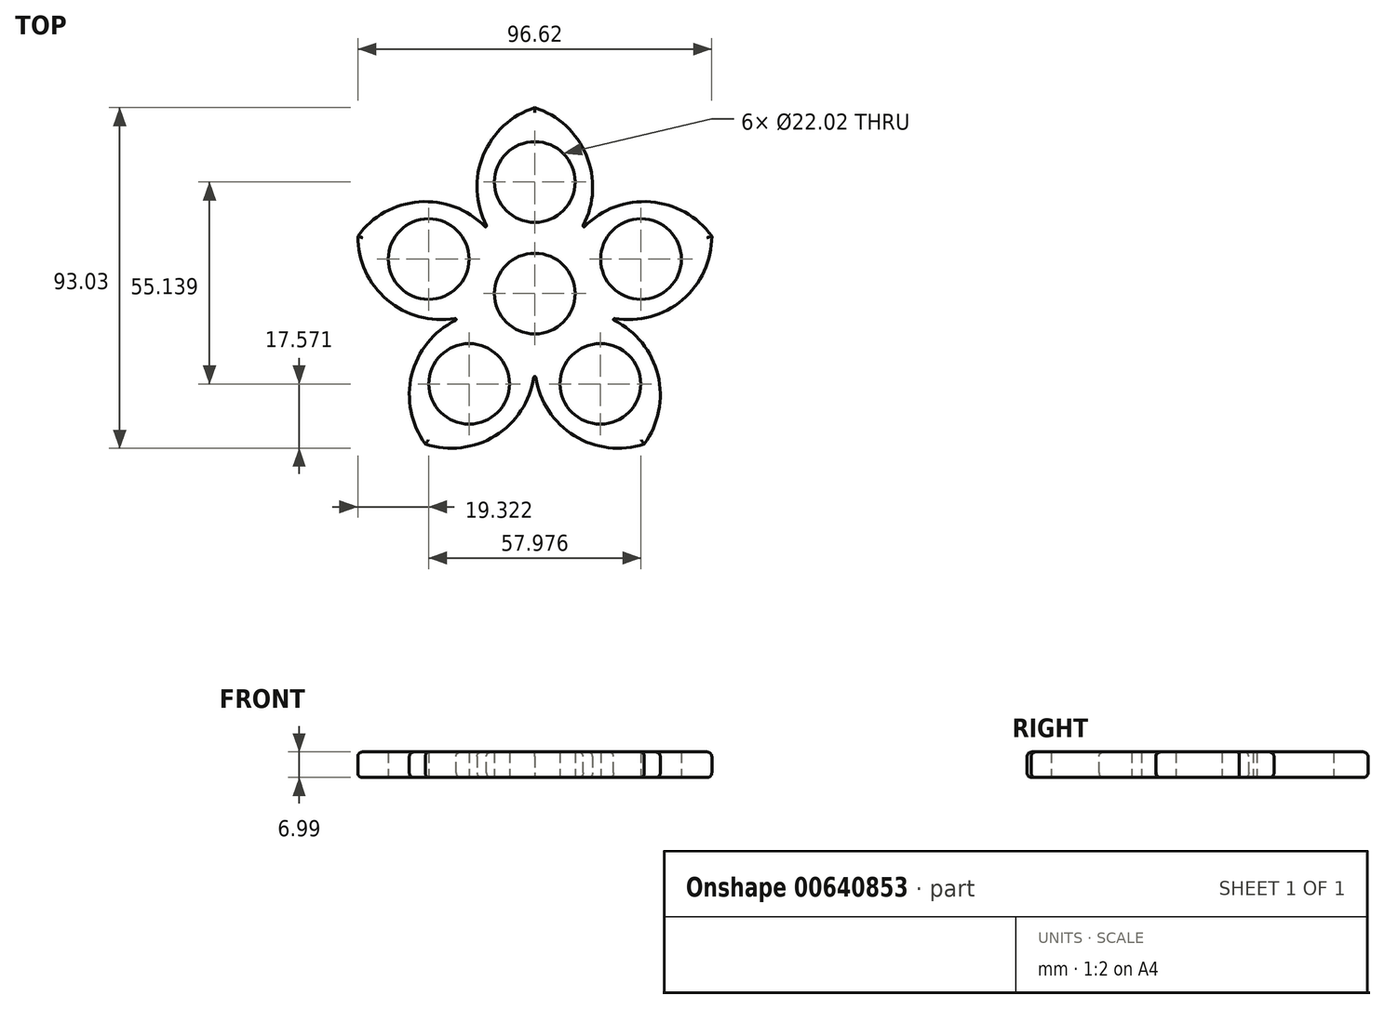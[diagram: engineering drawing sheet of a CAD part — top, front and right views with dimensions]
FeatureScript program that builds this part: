
annotation { "Feature Type Name" : "Feature", "Feature Type Description" : "" }
export const myFeature = defineFeature(function(context is Context, id is Id, definition is map)
    precondition{}
    {
        {
            var Q0;
            Q0=qCreatedBy(makeId("Top.planeOp"),FACE);
            var sketch = newSketch(context, id + "F0", { "sketchPlane" : qUnion([Q0])});
            skCircle(sketch, "E0", {"center": v(0, 0) * mm, "radius": 11.01 * mm});
            skCircle(sketch, "E1", {"center": v(0, 30.48) * mm, "radius": 11.01 * mm});
            skCircle(sketch, "E2", {"center": v(28.99, 9.42) * mm, "radius": 11.01 * mm});
            skCircle(sketch, "E3", {"center": v(17.92, -24.66) * mm, "radius": 11.01 * mm});
            skCircle(sketch, "E4", {"center": v(-17.92, -24.66) * mm, "radius": 11.01 * mm});
            skCircle(sketch, "E5", {"center": v(-28.99, 9.42) * mm, "radius": 11.01 * mm});
            skLineSegment(sketch, "E6", {"start": v(-28.99, 9.42) * mm, "end": v(0, 0) * mm});
            skLineSegment(sketch, "E7", {"start": v(0, 0) * mm, "end": v(0, 30.48) * mm});
            skLineSegment(sketch, "E8", {"start": v(28.99, 9.42) * mm, "end": v(0, 0) * mm});
            skLineSegment(sketch, "E9", {"start": v(-17.92, -24.66) * mm, "end": v(0, 0) * mm});
            skLineSegment(sketch, "E10", {"start": v(17.92, -24.66) * mm, "end": v(0, 0) * mm});
            skCircle(sketch, "E11", {"center": v(0, 0) * mm, "radius": 19.47 * mm});
            skLineSegment(sketch, "E12", {"start": v(0, 0) * mm, "end": v(0, -19.47) * mm});
            skLineSegment(sketch, "E13", {"start": v(0, -19.47) * mm, "end": v(0, 0) * mm});
            skLineSegment(sketch, "E14", {"start": v(0, 0) * mm, "end": v(18.52, -6.02) * mm});
            skLineSegment(sketch, "E15", {"start": v(18.52, -6.02) * mm, "end": v(0, 0) * mm});
            skLineSegment(sketch, "E16", {"start": v(-11.44, 15.75) * mm, "end": v(0, 0) * mm});
            skLineSegment(sketch, "E17", {"start": v(0, 0) * mm, "end": v(11.44, 15.75) * mm});
            skLineSegment(sketch, "E18", {"start": v(11.44, 15.75) * mm, "end": v(0, 0) * mm});
            skLineSegment(sketch, "E19", {"start": v(-18.52, -6.02) * mm, "end": v(0, 0) * mm});
            skLineSegment(sketch, "E20", {"start": v(0, 50.8) * mm, "end": v(0, 0) * mm});
            skLineSegment(sketch, "E21", {"start": v(0, 0) * mm, "end": v(-48.31, 15.7) * mm});
            skLineSegment(sketch, "E22", {"start": v(0, 0) * mm, "end": v(29.86, -41.1) * mm});
            skLineSegment(sketch, "E23", {"start": v(0, 0) * mm, "end": v(48.31, 15.7) * mm});
            skLineSegment(sketch, "E24", {"start": v(0, 0) * mm, "end": v(-29.86, -41.1) * mm});
            skArc(sketch, "E25", {"start": v(-48.31, 15.7) * mm, "mid": v(-38.96, -2.76) * mm, "end": v(-18.52, -6.02) * mm});
            skArc(sketch, "E26", {"start": v(-11.44, 15.75) * mm, "mid": v(-29.9, 25.13) * mm, "end": v(-48.31, 15.7) * mm});
            skArc(sketch, "E27", {"start": v(0, 50.8) * mm, "mid": v(-14.67, 36.2) * mm, "end": v(-11.44, 15.75) * mm});
            skArc(sketch, "E28", {"start": v(11.44, 15.75) * mm, "mid": v(14.67, 36.2) * mm, "end": v(0, 50.8) * mm});
            skArc(sketch, "E29", {"start": v(48.31, 15.7) * mm, "mid": v(29.9, 25.13) * mm, "end": v(11.44, 15.75) * mm});
            skArc(sketch, "E30", {"start": v(18.52, -6.02) * mm, "mid": v(38.96, -2.76) * mm, "end": v(48.31, 15.7) * mm});
            skArc(sketch, "E31", {"start": v(-18.52, -6.02) * mm, "mid": v(-33.14, -20.66) * mm, "end": v(-29.86, -41.1) * mm});
            skArc(sketch, "E32", {"start": v(-29.86, -41.1) * mm, "mid": v(-9.4, -37.9) * mm, "end": v(0, -19.47) * mm});
            skArc(sketch, "E33", {"start": v(0, -19.47) * mm, "mid": v(9.4, -37.9) * mm, "end": v(29.86, -41.1) * mm});
            skArc(sketch, "E34", {"start": v(29.86, -41.1) * mm, "mid": v(33.14, -20.66) * mm, "end": v(18.52, -6.02) * mm});
            skSolve(sketch);
        }
        {
            var Q0;
            Q0 = qSketchRegion(id + "F0", true);
            extrude(context, id + "F1", {"entities" : qUnion([Q0]), "depth" : 7 * mm, "offsetDistance" : 25.4 * mm});
        }
        {
            var Q0;
            Q0=makeQuery(id+"F1.opExtrude","SWEPT_EDGE",EDGE,{"disambiguationData":[OSD([sQuery(id+"F0.wireOp",EDGE,"E11"),sQuery(id+"F0.wireOp",EDGE,"E15"),sQuery(id+"F0.wireOp",EDGE,"E30"),sQuery(id+"F0.wireOp",EDGE,"E34")])]});
            var Q1;
            Q1=makeQuery(id+"F1.opExtrude","SWEPT_EDGE",EDGE,{"disambiguationData":[OSD([sQuery(id+"F0.wireOp",EDGE,"E11"),sQuery(id+"F0.wireOp",EDGE,"E18"),sQuery(id+"F0.wireOp",EDGE,"E28"),sQuery(id+"F0.wireOp",EDGE,"E29")])]});
            var Q2;
            Q2=makeQuery(id+"F1.opExtrude","SWEPT_EDGE",EDGE,{"disambiguationData":[OSD([sQuery(id+"F0.wireOp",EDGE,"E11"),sQuery(id+"F0.wireOp",EDGE,"E16"),sQuery(id+"F0.wireOp",EDGE,"E26"),sQuery(id+"F0.wireOp",EDGE,"E27")])]});
            var Q3;
            Q3=makeQuery(id+"F1.opExtrude","SWEPT_EDGE",EDGE,{"disambiguationData":[OSD([sQuery(id+"F0.wireOp",EDGE,"E11"),sQuery(id+"F0.wireOp",EDGE,"E19"),sQuery(id+"F0.wireOp",EDGE,"E25"),sQuery(id+"F0.wireOp",EDGE,"E31")])]});
            var Q4;
            Q4=makeQuery(id+"F1.opExtrude","SWEPT_EDGE",EDGE,{"disambiguationData":[OSD([sQuery(id+"F0.wireOp",EDGE,"E11"),sQuery(id+"F0.wireOp",EDGE,"E13"),sQuery(id+"F0.wireOp",EDGE,"E32"),sQuery(id+"F0.wireOp",EDGE,"E33")])]});
            fillet(context, id + "F2", {"entities" : qUnion([Q0, Q1, Q2, Q3, Q4]), "radius" : 0.25 * mm, "tangentPropagation" : true, "allowEdgeOverflow" : false});
        }
        {
            var Q0;
            Q0=makeQuery(id+"F1.opExtrude","CAP_EDGE",EDGE,{"disambiguationData":[OSD([sQuery(id+"F0.wireOp",EDGE,"E27")])],"isStart":false});
            var Q1;
            Q1=makeQuery(id+"F1.opExtrude","CAP_EDGE",EDGE,{"disambiguationData":[OSD([sQuery(id+"F0.wireOp",EDGE,"E28")])],"isStart":false});
            var Q2;
            Q2=makeQuery(id+"F1.opExtrude","CAP_EDGE",EDGE,{"disambiguationData":[OSD([sQuery(id+"F0.wireOp",EDGE,"E29")])],"isStart":false});
            var Q3;
            Q3=makeQuery(id+"F1.opExtrude","CAP_EDGE",EDGE,{"disambiguationData":[OSD([sQuery(id+"F0.wireOp",EDGE,"E30")])],"isStart":false});
            var Q4;
            Q4=makeQuery(id+"F1.opExtrude","CAP_EDGE",EDGE,{"disambiguationData":[OSD([sQuery(id+"F0.wireOp",EDGE,"E34")])],"isStart":false});
            var Q5;
            Q5=makeQuery(id+"F1.opExtrude","CAP_EDGE",EDGE,{"disambiguationData":[OSD([sQuery(id+"F0.wireOp",EDGE,"E33")])],"isStart":false});
            var Q6;
            Q6=makeQuery(id+"F1.opExtrude","CAP_EDGE",EDGE,{"disambiguationData":[OSD([sQuery(id+"F0.wireOp",EDGE,"E32")])],"isStart":false});
            var Q7;
            Q7=makeQuery(id+"F1.opExtrude","CAP_EDGE",EDGE,{"disambiguationData":[OSD([sQuery(id+"F0.wireOp",EDGE,"E31")])],"isStart":false});
            var Q8;
            Q8=makeQuery(id+"F1.opExtrude","CAP_EDGE",EDGE,{"disambiguationData":[OSD([sQuery(id+"F0.wireOp",EDGE,"E25")])],"isStart":false});
            var Q9;
            Q9=makeQuery(id+"F1.opExtrude","CAP_EDGE",EDGE,{"disambiguationData":[OSD([sQuery(id+"F0.wireOp",EDGE,"E26")])],"isStart":false});
            fillet(context, id + "F3", {"entities" : qUnion([Q0, Q1, Q2, Q3, Q4, Q5, Q6, Q7, Q8, Q9]), "radius" : 1.27 * mm, "tangentPropagation" : true, "allowEdgeOverflow" : false});
        }
        {
            var Q0;
            Q0=makeQuery(id+"F1.opExtrude","CAP_EDGE",EDGE,{"disambiguationData":[OSD([sQuery(id+"F0.wireOp",EDGE,"E25")])],"isStart":true});
            var Q1;
            Q1=makeQuery(id+"F1.opExtrude","CAP_EDGE",EDGE,{"disambiguationData":[OSD([sQuery(id+"F0.wireOp",EDGE,"E26")])],"isStart":true});
            var Q2;
            Q2=makeQuery(id+"F1.opExtrude","CAP_EDGE",EDGE,{"disambiguationData":[OSD([sQuery(id+"F0.wireOp",EDGE,"E27")])],"isStart":true});
            var Q3;
            Q3=makeQuery(id+"F1.opExtrude","CAP_EDGE",EDGE,{"disambiguationData":[OSD([sQuery(id+"F0.wireOp",EDGE,"E28")])],"isStart":true});
            var Q4;
            Q4=makeQuery(id+"F1.opExtrude","CAP_EDGE",EDGE,{"disambiguationData":[OSD([sQuery(id+"F0.wireOp",EDGE,"E29")])],"isStart":true});
            var Q5;
            Q5=makeQuery(id+"F1.opExtrude","CAP_EDGE",EDGE,{"disambiguationData":[OSD([sQuery(id+"F0.wireOp",EDGE,"E30")])],"isStart":true});
            var Q6;
            Q6=makeQuery(id+"F1.opExtrude","CAP_EDGE",EDGE,{"disambiguationData":[OSD([sQuery(id+"F0.wireOp",EDGE,"E34")])],"isStart":true});
            var Q7;
            Q7=makeQuery(id+"F1.opExtrude","CAP_EDGE",EDGE,{"disambiguationData":[OSD([sQuery(id+"F0.wireOp",EDGE,"E33")])],"isStart":true});
            var Q8;
            Q8=makeQuery(id+"F1.opExtrude","CAP_EDGE",EDGE,{"disambiguationData":[OSD([sQuery(id+"F0.wireOp",EDGE,"E32")])],"isStart":true});
            fillet(context, id + "F4", {"entities" : qUnion([Q0, Q1, Q2, Q3, Q4, Q5, Q6, Q7, Q8]), "radius" : 1.27 * mm, "tangentPropagation" : true, "allowEdgeOverflow" : false});
        }
    });
